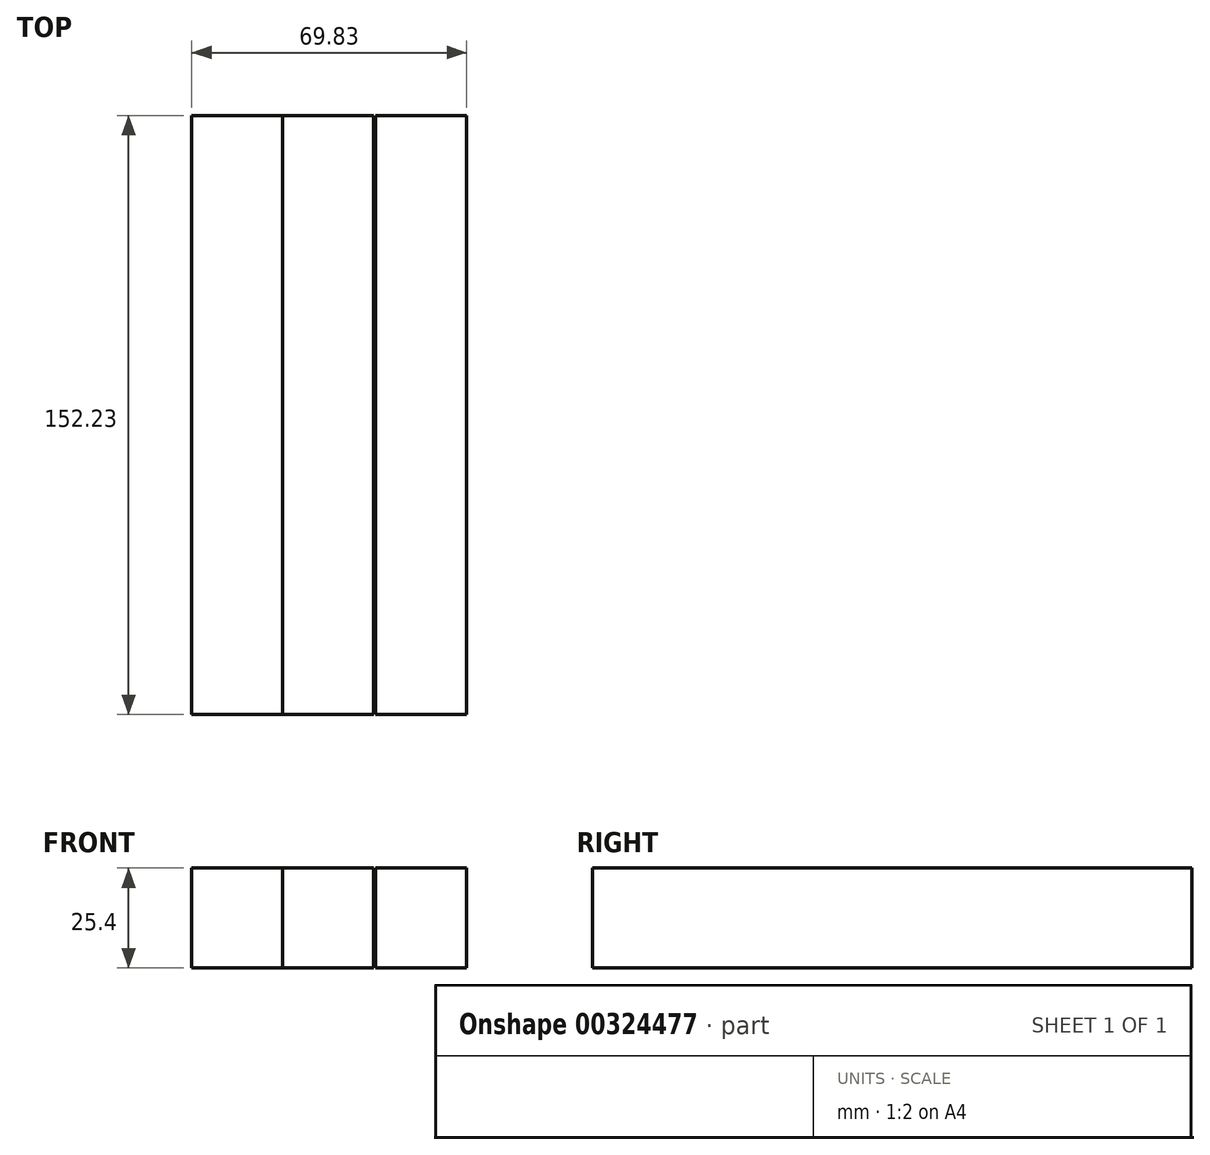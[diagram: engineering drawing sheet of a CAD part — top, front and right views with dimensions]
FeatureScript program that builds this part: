
annotation { "Feature Type Name" : "Feature", "Feature Type Description" : "" }
export const myFeature = defineFeature(function(context is Context, id is Id, definition is map)
    precondition{}
    {
        {
            var Q0;
            Q0=qCreatedBy(makeId("Top.planeOp"),FACE);
            var sketch = newSketch(context, id + "F0", { "sketchPlane" : qUnion([Q0])});
            skLineSegment(sketch, "E0.bottom", {"start": v(-76.39, 75.71) * mm, "end": v(-53.3, 75.71) * mm});
            skLineSegment(sketch, "E0.top", {"start": v(-76.39, -76.52) * mm, "end": v(-53.3, -76.52) * mm});
            skLineSegment(sketch, "E0.left", {"start": v(-76.39, 75.71) * mm, "end": v(-76.39, -76.52) * mm});
            skLineSegment(sketch, "E0.right", {"start": v(-53.3, 75.71) * mm, "end": v(-53.3, -76.52) * mm});
            skSolve(sketch);
        }
        {
            var Q0;
            Q0 = qSketchRegion(id + "F0", true);
            extrude(context, id + "F1", {"entities" : qUnion([Q0]), "depth" : 25.4 * mm});
        }
        {
            var Q0;
            Q0=makeQuery(id+"F1.opExtrude","SWEPT_BODY",BODY,{"disambiguationData":[OSD([sQuery(id+"F0.wireOp",EDGE,"E0.bottom"),sQuery(id+"F0.wireOp",EDGE,"E0.top"),sQuery(id+"F0.wireOp",EDGE,"E0.left"),sQuery(id+"F0.wireOp",EDGE,"E0.right")])]});
            transform(context, id + "F2", {"entities" : qUnion([Q0]), "transformType" : TransformType.TRANSLATION_3D, "dx" : 23.1 * mm, "dy" : 0 * mm, "dz" : 0 * mm, "makeCopy" : true});
        }
        {
            var Q0;
            Q0=makeQuery(id+"F2.opPattern","COPY",BODY,{"derivedFrom":makeQuery(id+"F1.opExtrude","SWEPT_BODY",BODY,{"disambiguationData":[OSD([sQuery(id+"F0.wireOp",EDGE,"E0.bottom"),sQuery(id+"F0.wireOp",EDGE,"E0.top"),sQuery(id+"F0.wireOp",EDGE,"E0.left"),sQuery(id+"F0.wireOp",EDGE,"E0.right")])]}),"instanceName":"1"});
            transform(context, id + "F3", {"entities" : qUnion([Q0]), "transformType" : TransformType.TRANSLATION_3D, "dx" : 23.62 * mm, "dy" : 0 * mm, "dz" : 0 * mm, "makeCopy" : true});
        }
    });
